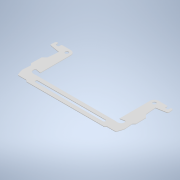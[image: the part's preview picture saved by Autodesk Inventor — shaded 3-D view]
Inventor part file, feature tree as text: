
AUTODESK INVENTOR PART (.ipt)
format: ipt  version: 2022 (Build 260153000, 153)  size: 214,016 bytes
history: native  units: mm
features: other x1, extrude x1, sketch x1
ambient origin geometry x8: Origin, YZ Plane, XZ Plane, XY Plane, X Axis, Y Axis, Z Axis, Center Point
bodies: Body1 (feature_tree)
feature tree (3):
  other  "Твердое тело1"
  extrude  "Выдавливание1"  Depth=0.5mm TaperAngle=0.0deg
  sketch  "Эскиз1"
